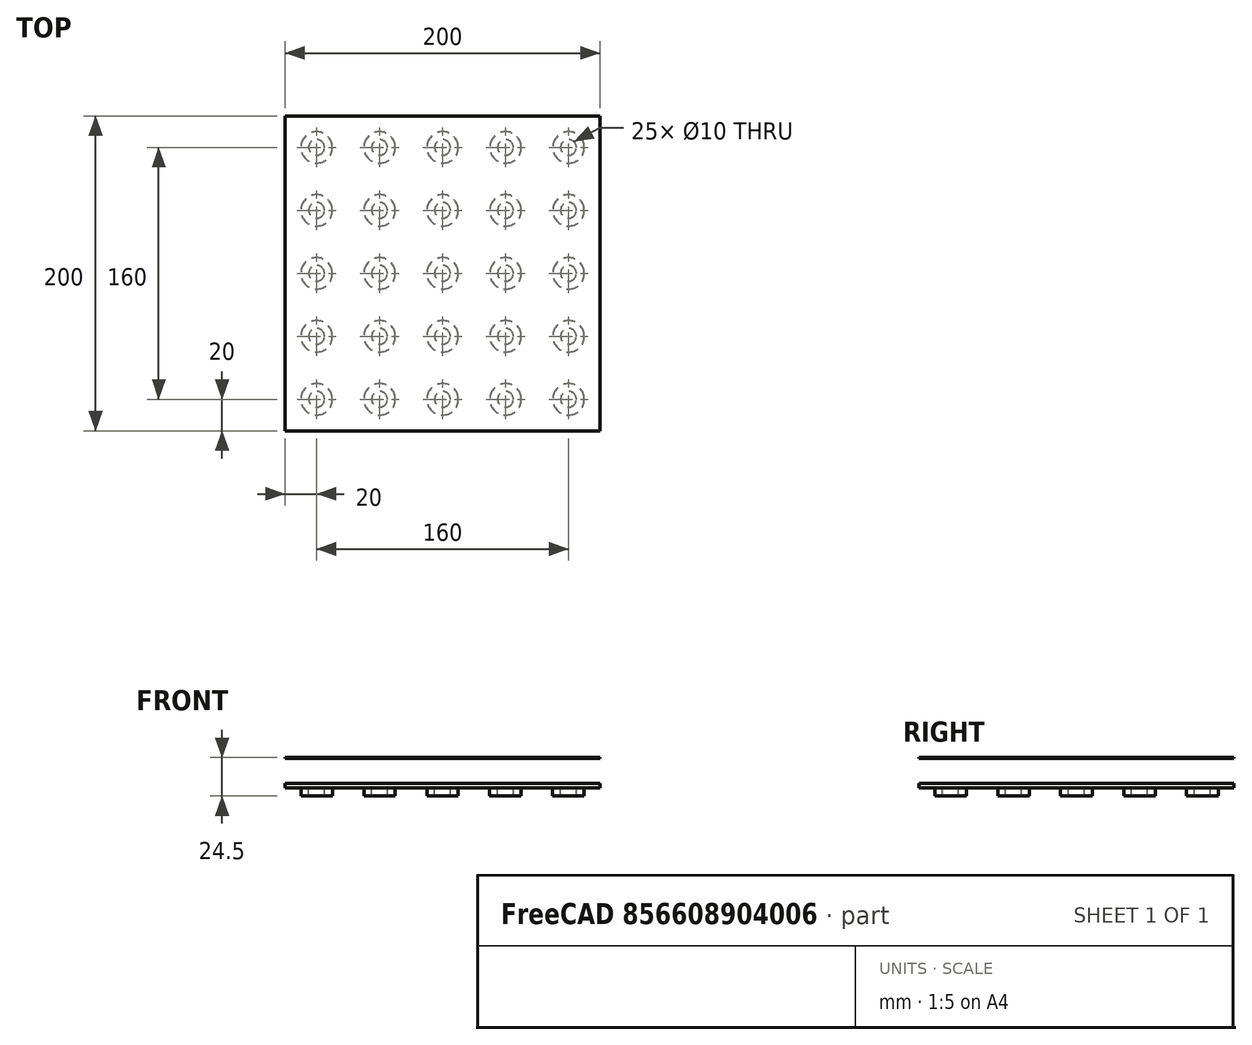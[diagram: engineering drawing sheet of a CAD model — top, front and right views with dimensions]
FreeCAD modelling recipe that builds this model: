
FCSTD DOCUMENT  (FreeCAD 0.18.4R)
Label: Solenoid-bed
License: All rights reserved
LicenseURL: http://en.wikipedia.org/wiki/All_rights_reserved
objects: Part::Feature×16, Part::MultiFuse×4, Part::Cylinder×3, Part::Box×2, Part::Cut×1
note: 26 computed .brp shape members not serialized (recipe doc carries the construction recipe); baked Part::Feature solids carry a one-line shape summary decoded from their .brp

FEATURE [Part::Box] Box  label="aluminium-bed"
  AttacherType = Attacher::AttachEngine3D
  Height = 3
  Length = 200
  Placement = pos=(0,0,5) rot=(0,0,1;0rad)
  Width = 200
FEATURE [Part::Cylinder] Cylinder  label="ferrite-or-soft-iron"
  Angle = 360
  AttacherType = Attacher::AttachEngine3D
  Height = 5
  Placement = pos=(20,20,0) rot=(0,0,1;0rad)
  Radius = 5
FEATURE [Part::Cylinder] Cylinder001
  Angle = 360
  AttacherType = Attacher::AttachEngine3D
  Height = 5
  Radius = 10
FEATURE [Part::Cylinder] Cylinder002
  Angle = 360
  AttacherType = Attacher::AttachEngine3D
  Height = 8
  Placement = pos=(0,0,-1) rot=(0,0,1;0rad)
  Radius = 5
FEATURE [Part::Cut] Cut  label="solenoid-and-heater"
  Base = -> Cylinder001
  Placement = pos=(20,20,0) rot=(0,0,1;0rad)
  Tool = -> Cylinder002
FEATURE [Part::Box] Box001  label="aluminium-bed001"
  AttacherType = Attacher::AttachEngine3D
  Height = 0.5
  Length = 200
  Placement = pos=(0,0,24) rot=(0,0,1;0rad)
  Width = 200
FEATURE [Part::Feature] Cylinder003 .. Cylinder006  x4 (patterned run collapsed; names and placements below)
  shape: bbox 10 x 10 x 5 mm, 3 faces (baked)
  placements: 4 in arithmetic series — first pos=(60,20,0) rot=(0,0,1;0rad), step (40,0,0), last pos=(180,20,0) rot=(0,0,1;0rad)
FEATURE [Part::Feature] Cut001 .. Cut004  x4 (patterned run collapsed; names and placements below)
  shape: bbox 20 x 20 x 5 mm, 4 faces (baked)
  placements: 4 in arithmetic series — first pos=(60,20,0) rot=(0,0,1;0rad), step (40,0,0), last pos=(180,20,0) rot=(0,0,1;0rad)
FEATURE [Part::MultiFuse] Fusion  label="cores-1"
  Shapes = -> [Cylinder,Cylinder003,Cylinder004,Cylinder005,Cylinder006]
FEATURE [Part::MultiFuse] Fusion001  label="coils-1"
  Shapes = -> [Cut,Cut001,Cut002,Cut003,Cut004]
FEATURE [Part::Feature] Fusion002 .. Fusion005  x4 (patterned run collapsed; names and placements below)
  shape: bbox 170 x 10 x 5 mm, 15 faces, 5 solids (baked)
  placements: 4 in arithmetic series — first pos=(0,40,0) rot=(0,0,1;0rad), step (0,40,0), last pos=(0,160,0) rot=(0,0,1;0rad)
FEATURE [Part::Feature] Fusion001001 .. Fusion001004  x4 (patterned run collapsed; names and placements below)
  shape: bbox 180 x 20 x 5 mm, 20 faces, 5 solids (baked)
  placements: 4 in arithmetic series — first pos=(0,40,0) rot=(0,0,1;0rad), step (0,40,0), last pos=(0,160,0) rot=(0,0,1;0rad)
FEATURE [Part::MultiFuse] Fusion001005  label="cores"
  Shapes = -> [Fusion,Fusion002,Fusion003,Fusion004,Fusion005]
FEATURE [Part::MultiFuse] Fusion001006  label="coils"
  Shapes = -> [Fusion001,Fusion001004,Fusion001003,Fusion001002,Fusion001001]
